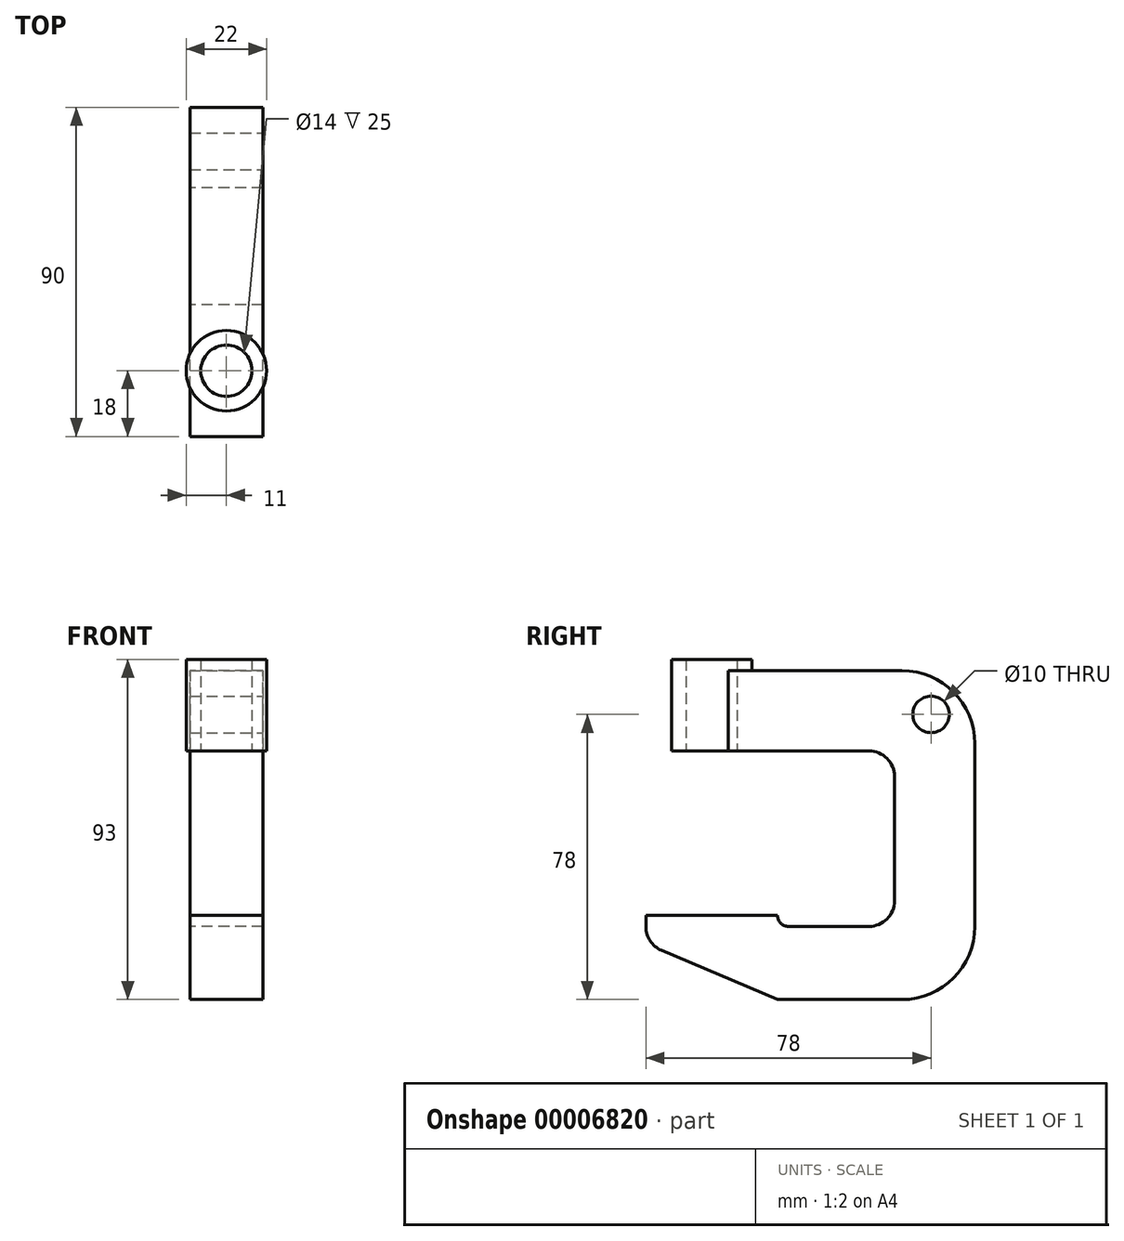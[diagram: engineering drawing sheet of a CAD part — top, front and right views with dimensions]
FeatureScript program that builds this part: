
annotation { "Feature Type Name" : "Feature", "Feature Type Description" : "" }
export const myFeature = defineFeature(function(context is Context, id is Id, definition is map)
    precondition{}
    {
        {
            var Q0;
            Q0=qCreatedBy(makeId("Right.planeOp"),FACE);
            var sketch = newSketch(context, id + "F0", { "sketchPlane" : qUnion([Q0])});
            skLineSegment(sketch, "E0", {"start": v(0, 0) * mm, "end": v(0, -3.09) * mm});
            skLineSegment(sketch, "E1", {"start": v(4.26, -9.53) * mm, "end": v(36, -23) * mm});
            skLineSegment(sketch, "E2", {"start": v(36, -23) * mm, "end": v(70, -23) * mm});
            skLineSegment(sketch, "E3", {"start": v(90, -3) * mm, "end": v(90, 47) * mm});
            skLineSegment(sketch, "E4", {"start": v(70, 67) * mm, "end": v(7, 67) * mm});
            skLineSegment(sketch, "E5", {"start": v(7, 67) * mm, "end": v(7, 45) * mm});
            skLineSegment(sketch, "E6", {"start": v(7, 45) * mm, "end": v(61, 45) * mm});
            skLineSegment(sketch, "E7", {"start": v(68, 38) * mm, "end": v(68, 4) * mm});
            skLineSegment(sketch, "E8", {"start": v(61, -3) * mm, "end": v(36, -3) * mm});
            skLineSegment(sketch, "E9", {"start": v(36, -3) * mm, "end": v(36, 0) * mm});
            skLineSegment(sketch, "E10", {"start": v(36, 0) * mm, "end": v(0, 0) * mm});
            skLineSegment(sketch, "E11", {"start": v(36, -23) * mm, "end": v(21.85, -23) * mm, "construction": true});
            skPoint(sketch, "E12.visualSharp", {"position": v(90, -23) * mm});
            skArc(sketch, "E12.filletArc", {"start": v(70, -23) * mm, "mid": v(84.14, -17.14) * mm, "end": v(90, -3) * mm});
            skPoint(sketch, "E13.visualSharp", {"position": v(90, 67) * mm});
            skArc(sketch, "E13.filletArc", {"start": v(90, 47) * mm, "mid": v(84.14, 61.14) * mm, "end": v(70, 67) * mm});
            skPoint(sketch, "E14.visualSharp", {"position": v(68, 45) * mm});
            skArc(sketch, "E14.filletArc", {"start": v(68, 38) * mm, "mid": v(65.95, 42.95) * mm, "end": v(61, 45) * mm});
            skPoint(sketch, "E15.visualSharp", {"position": v(68, -3) * mm});
            skArc(sketch, "E15.filletArc", {"start": v(61, -3) * mm, "mid": v(65.95, -0.95) * mm, "end": v(68, 4) * mm});
            skPoint(sketch, "E16.visualSharp", {"position": v(0, -7.72) * mm});
            skArc(sketch, "E16.filletArc", {"start": v(0, -3.09) * mm, "mid": v(1.16, -6.95) * mm, "end": v(4.26, -9.53) * mm});
            skSolve(sketch);
        }
        {
            var Q0;
            Q0 = qSketchRegion(id + "F0", true);
            extrude(context, id + "F1", {"entities" : qUnion([Q0]), "endBound" : BoundingType.SYMMETRIC, "depth" : 20 * mm});
        }
        {
            var Q0;
            Q0=makeQuery(id+"F1.opExtrude","SWEPT_FACE",FACE,{"disambiguationData":[OSD([sQuery(id+"F0.wireOp",EDGE,"E6")])]});
            var sketch = newSketch(context, id + "F2", { "sketchPlane" : qUnion([Q0])});
            skCircle(sketch, "E17", {"center": v(0, -18) * mm, "radius": 11 * mm});
            skCircle(sketch, "E18", {"center": v(0, -18) * mm, "radius": 7 * mm});
            skSolve(sketch);
        }
        {
            var Q0;
            Q0 = qSketchRegion(id + "F2", true);
            extrude(context, id + "F3", {"entities" : qUnion([Q0]), "operationType" : NewBodyOperationType.ADD, "oppositeDirection" : true, "depth" : 25 * mm});
        }
        {
            var Q0;
            Q0=makeQuery(id+"F3.boolean.opBoolean","SPLIT",FACE,{"disambiguationData":[TD([makeQuery(id+"F3.opExtrude","SWEPT_FACE",FACE,{"disambiguationData":[OSD([sQuery(id+"F2.wireOp",EDGE,"E18")])]})])],"derivedFrom":makeQuery(id+"F1.opExtrude","SWEPT_FACE",FACE,{"disambiguationData":[OSD([sQuery(id+"F0.wireOp",EDGE,"E4")])]})});
            var sketch = newSketch(context, id + "F4", { "sketchPlane" : qUnion([Q0])});
            skCircle(sketch, "E19.0", {"center": v(0, 18) * mm, "radius": 7 * mm});
            skSolve(sketch);
        }
        {
            var Q0;
            Q0 = qSketchRegion(id + "F4", true);
            extrude(context, id + "F5", {"entities" : qUnion([Q0]), "operationType" : NewBodyOperationType.REMOVE, "oppositeDirection" : true, "depth" : 25 * mm});
        }
        {
            var Q0;
            {var subQ0=sQuery(id+"F0.wireOp",EDGE,"E4");var subQ1=makeQuery(id+"F1.opExtrude","SWEPT_FACE",FACE,{"disambiguationData":[OSD([subQ0])]});var subQ2=sQuery(id+"F0.wireOp",EDGE,"E5");Q0=makeQuery(id+"F3.boolean.opBoolean","SPLIT",FACE,{"disambiguationData":[TD([makeQuery(id+"F1.opExtrude","CAP_FACE",FACE,{"disambiguationData":[OSD([sQuery(id+"F0.wireOp",EDGE,"E0"),sQuery(id+"F0.wireOp",EDGE,"E1"),sQuery(id+"F0.wireOp",EDGE,"E2"),sQuery(id+"F0.wireOp",EDGE,"E3"),subQ0,subQ2,sQuery(id+"F0.wireOp",EDGE,"E6"),sQuery(id+"F0.wireOp",EDGE,"E7"),sQuery(id+"F0.wireOp",EDGE,"E8"),sQuery(id+"F0.wireOp",EDGE,"E9"),sQuery(id+"F0.wireOp",EDGE,"E10"),sQuery(id+"F0.wireOp",EDGE,"E12.filletArc"),sQuery(id+"F0.wireOp",EDGE,"E13.filletArc"),sQuery(id+"F0.wireOp",EDGE,"E14.filletArc"),sQuery(id+"F0.wireOp",EDGE,"E15.filletArc"),sQuery(id+"F0.wireOp",EDGE,"E16.filletArc")])],"isStart":false}),subQ1,makeQuery(id+"F1.opExtrude","SWEPT_FACE",FACE,{"disambiguationData":[OSD([subQ2])]}),makeQuery(id+"F3.opExtrude","SWEPT_FACE",FACE,{"disambiguationData":[OSD([sQuery(id+"F2.wireOp",EDGE,"E17")])]})])],"derivedFrom":subQ1});}
            var sketch = newSketch(context, id + "F6", { "sketchPlane" : qUnion([Q0])});
            skLineSegment(sketch, "E20.1.0", {"start": v(-10, 7) * mm, "end": v(0, 7) * mm});
            skArc(sketch, "E20.1.1", {"start": v(0, 7) * mm, "mid": v(-5.94, 8.74) * mm, "end": v(-10, 13.42) * mm});
            skLineSegment(sketch, "E20.1.2", {"start": v(-10, 13.42) * mm, "end": v(-10, 7) * mm});
            skSolve(sketch);
        }
        {
            var Q0;
            Q0 = qSketchRegion(id + "F6", true);
            extrude(context, id + "F7", {"entities" : qUnion([Q0]), "operationType" : NewBodyOperationType.REMOVE, "oppositeDirection" : true, "depth" : 25 * mm});
        }
        {
            var Q0;
            {var subQ0=sQuery(id+"F0.wireOp",EDGE,"E4");var subQ1=makeQuery(id+"F1.opExtrude","SWEPT_FACE",FACE,{"disambiguationData":[OSD([subQ0])]});var subQ2=sQuery(id+"F0.wireOp",EDGE,"E5");Q0=makeQuery(id+"F3.boolean.opBoolean","SPLIT",FACE,{"disambiguationData":[TD([makeQuery(id+"F1.opExtrude","CAP_FACE",FACE,{"disambiguationData":[OSD([sQuery(id+"F0.wireOp",EDGE,"E0"),sQuery(id+"F0.wireOp",EDGE,"E1"),sQuery(id+"F0.wireOp",EDGE,"E2"),sQuery(id+"F0.wireOp",EDGE,"E3"),subQ0,subQ2,sQuery(id+"F0.wireOp",EDGE,"E6"),sQuery(id+"F0.wireOp",EDGE,"E7"),sQuery(id+"F0.wireOp",EDGE,"E8"),sQuery(id+"F0.wireOp",EDGE,"E9"),sQuery(id+"F0.wireOp",EDGE,"E10"),sQuery(id+"F0.wireOp",EDGE,"E12.filletArc"),sQuery(id+"F0.wireOp",EDGE,"E13.filletArc"),sQuery(id+"F0.wireOp",EDGE,"E14.filletArc"),sQuery(id+"F0.wireOp",EDGE,"E15.filletArc"),sQuery(id+"F0.wireOp",EDGE,"E16.filletArc")])],"isStart":false}),subQ1,makeQuery(id+"F1.opExtrude","SWEPT_FACE",FACE,{"disambiguationData":[OSD([subQ2])]}),makeQuery(id+"F3.opExtrude","SWEPT_FACE",FACE,{"disambiguationData":[OSD([sQuery(id+"F2.wireOp",EDGE,"E17")])]})])],"derivedFrom":subQ1});}
            var sketch = newSketch(context, id + "F8", { "sketchPlane" : qUnion([Q0])});
            skArc(sketch, "E21.0", {"start": v(10, 13.42) * mm, "mid": v(5.94, 8.74) * mm, "end": v(0, 7) * mm});
            skLineSegment(sketch, "E22", {"start": v(10, 13.42) * mm, "end": v(10, 7) * mm});
            skLineSegment(sketch, "E23", {"start": v(10, 7) * mm, "end": v(0, 7) * mm});
            skSolve(sketch);
        }
        {
            var Q0;
            Q0 = qSketchRegion(id + "F8", true);
            extrude(context, id + "F9", {"entities" : qUnion([Q0]), "operationType" : NewBodyOperationType.REMOVE, "oppositeDirection" : true, "depth" : 25 * mm});
        }
        {
            var Q0;
            Q0=makeQuery(id+"F1.opExtrude","SWEPT_EDGE",EDGE,{"disambiguationData":[OSD([sQuery(id+"F0.wireOp",EDGE,"E8"),sQuery(id+"F0.wireOp",EDGE,"E9")])]});
            fillet(context, id + "F10", {"entities" : qUnion([Q0]), "radius" : 3 * mm, "tangentPropagation" : true, "allowEdgeOverflow" : false});
        }
        {
            var Q0;
            Q0=qCreatedBy(makeId("Right.planeOp"),FACE);
            var sketch = newSketch(context, id + "F11", { "sketchPlane" : qUnion([Q0])});
            skLineSegment(sketch, "E24", {"start": v(11, 100) * mm, "end": v(7, 100) * mm});
            skLineSegment(sketch, "E25", {"start": v(7, 100) * mm, "end": v(7, 118) * mm});
            skLineSegment(sketch, "E26", {"start": v(7, 118) * mm, "end": v(18, 118) * mm});
            skLineSegment(sketch, "E27", {"start": v(18, 118) * mm, "end": v(18, 35) * mm});
            skLineSegment(sketch, "E28", {"start": v(11, 100) * mm, "end": v(11, 35) * mm});
            skLineSegment(sketch, "E29", {"start": v(11, 35) * mm, "end": v(18, 35) * mm});
            skSolve(sketch);
        }
        {
            var Q0;
            Q0 = qSketchRegion(id + "F11", true);
            var Q1;
            Q1=sQuery(id+"F11.wireOp",EDGE,"E27");
            revolve(context, id + "F12", {"entities" : qUnion([Q0]), "axis" : qUnion([Q1]), "revolveType" : RevolveType.FULL});
        }
        {
            var Q0;
            Q0=makeQuery(id+"F12.opRevolve","SWEPT_EDGE",EDGE,{"disambiguationData":[OSD([sQuery(id+"F11.wireOp",EDGE,"E25"),sQuery(id+"F11.wireOp",EDGE,"E26")])]});
            chamfer(context, id + "F13", {"entities" : qUnion([Q0]), "width" : 2 * mm, "tangentPropagation" : true});
        }
        {
            var Q0;
            Q0=makeQuery(id+"F12.opRevolve","SWEPT_FACE",FACE,{"disambiguationData":[OSD([sQuery(id+"F11.wireOp",EDGE,"E29")])]});
            var sketch = newSketch(context, id + "F14", { "sketchPlane" : qUnion([Q0])});
            skCircle(sketch, "E30", {"center": v(0, -18) * mm, "radius": 5 * mm});
            skSolve(sketch);
        }
        {
            var Q0;
            Q0 = qSketchRegion(id + "F14", true);
            extrude(context, id + "F15", {"entities" : qUnion([Q0]), "operationType" : NewBodyOperationType.ADD, "depth" : 2 * mm});
        }
        {
            var Q0;
            Q0=makeQuery(id+"F15.opExtrude","CAP_FACE",FACE,{"disambiguationData":[OSD([sQuery(id+"F14.wireOp",EDGE,"E30")])],"isStart":false});
            var sketch = newSketch(context, id + "F16", { "sketchPlane" : qUnion([Q0])});
            skCircle(sketch, "E31", {"center": v(0, -18) * mm, "radius": 3 * mm});
            skSolve(sketch);
        }
        {
            var Q0;
            Q0 = qSketchRegion(id + "F16", true);
            extrude(context, id + "F17", {"entities" : qUnion([Q0]), "operationType" : NewBodyOperationType.ADD, "depth" : 8 * mm});
        }
        {
            var Q0;
            Q0=qCreatedBy(makeId("Right.planeOp"),FACE);
            var sketch = newSketch(context, id + "F18", { "sketchPlane" : qUnion([Q0])});
            skCircle(sketch, "E32", {"center": v(18, 109) * mm, "radius": 5 * mm});
            skSolve(sketch);
        }
        {
            var Q0;
            Q0 = qSketchRegion(id + "F18", true);
            extrude(context, id + "F19", {"entities" : qUnion([Q0]), "operationType" : NewBodyOperationType.REMOVE, "oppositeDirection" : true, "depth" : 25 * mm});
        }
        {
            var Q0;
            Q0=makeQuery(id+"F19.boolean.opBoolean","COPY",FACE,{"derivedFrom":makeQuery(id+"F19.opExtrude","CAP_FACE",FACE,{"disambiguationData":[OSD([sQuery(id+"F18.wireOp",EDGE,"E32")])],"isStart":true})});
            var sketch = newSketch(context, id + "F20", { "sketchPlane" : qUnion([Q0])});
            skCircle(sketch, "E33.0", {"center": v(-18, 109) * mm, "radius": 5 * mm});
            skSolve(sketch);
        }
        {
            var Q0;
            Q0 = qSketchRegion(id + "F20", true);
            extrude(context, id + "F21", {"entities" : qUnion([Q0]), "operationType" : NewBodyOperationType.REMOVE, "oppositeDirection" : true, "depth" : 25 * mm});
        }
        {
            var Q0;
            Q0=qCreatedBy(makeId("Right.planeOp"),FACE);
            var sketch = newSketch(context, id + "F22", { "sketchPlane" : qUnion([Q0])});
            skCircle(sketch, "E34.0", {"center": v(18, 109) * mm, "radius": 5 * mm});
            skSolve(sketch);
        }
        {
            var Q0;
            Q0 = qSketchRegion(id + "F22", true);
            extrude(context, id + "F23", {"entities" : qUnion([Q0]), "endBound" : BoundingType.SYMMETRIC, "depth" : 89 * mm});
        }
        {
            var Q0;
            Q0=makeQuery(id+"F23.opExtrude","CAP_FACE",FACE,{"disambiguationData":[OSD([sQuery(id+"F22.wireOp",EDGE,"E34.0")])],"isStart":false});
            var sketch = newSketch(context, id + "F24", { "sketchPlane" : qUnion([Q0])});
            skCircle(sketch, "E35", {"center": v(18, 109) * mm, "radius": 3 * mm});
            skSolve(sketch);
        }
        {
            var Q0;
            Q0 = qSketchRegion(id + "F24", true);
            extrude(context, id + "F25", {"entities" : qUnion([Q0]), "operationType" : NewBodyOperationType.ADD, "depth" : 12 * mm});
        }
        {
            var Q0;
            Q0=makeQuery(id+"F23.opExtrude","CAP_FACE",FACE,{"disambiguationData":[OSD([sQuery(id+"F22.wireOp",EDGE,"E34.0")])],"isStart":true});
            var sketch = newSketch(context, id + "F26", { "sketchPlane" : qUnion([Q0])});
            skCircle(sketch, "E36", {"center": v(-18, 109) * mm, "radius": 3 * mm});
            skSolve(sketch);
        }
        {
            var Q0;
            Q0 = qSketchRegion(id + "F26", true);
            extrude(context, id + "F27", {"entities" : qUnion([Q0]), "operationType" : NewBodyOperationType.ADD, "depth" : 12 * mm});
        }
        {
            var Q0;
            Q0=makeQuery(id+"F25.opExtrude","CAP_FACE",FACE,{"disambiguationData":[OSD([sQuery(id+"F24.wireOp",EDGE,"E35")])],"isStart":false});
            var sketch = newSketch(context, id + "F28", { "sketchPlane" : qUnion([Q0])});
            skCircle(sketch, "E37.0", {"center": v(18, 109) * mm, "radius": 3 * mm});
            skCircle(sketch, "E38", {"center": v(18, 109) * mm, "radius": 10 * mm});
            skSolve(sketch);
        }
        {
            var Q0;
            Q0 = qSketchRegion(id + "F28", true);
            extrude(context, id + "F29", {"entities" : qUnion([Q0]), "oppositeDirection" : true, "depth" : 10 * mm});
        }
        {
            var Q0;
            Q0=makeQuery(id+"F29.opExtrude","CAP_EDGE",EDGE,{"disambiguationData":[OSD([sQuery(id+"F28.wireOp",EDGE,"E38")])],"isStart":true});
            var Q1;
            Q1=makeQuery(id+"F29.opExtrude","CAP_EDGE",EDGE,{"disambiguationData":[OSD([sQuery(id+"F28.wireOp",EDGE,"E38")])],"isStart":false});
            chamfer(context, id + "F30", {"entities" : qUnion([Q0, Q1]), "width" : 2 * mm, "tangentPropagation" : true});
        }
        {
            var Q0;
            Q0=makeQuery(id+"F29.opExtrude","SWEPT_BODY",BODY,{"disambiguationData":[OSD([sQuery(id+"F28.wireOp",EDGE,"E37.0"),sQuery(id+"F28.wireOp",EDGE,"E38")])]});
            var Q1;
            Q1=qCreatedBy(makeId("Right.planeOp"),FACE);
            mirror(context, id + "F31", {"entities" : qUnion([Q0]), "mirrorPlane" : qUnion([Q1])});
        }
        {
            var Q0;
            Q0=qCreatedBy(makeId("Right.planeOp"),FACE);
            var sketch = newSketch(context, id + "F32", { "sketchPlane" : qUnion([Q0])});
            skLineSegment(sketch, "E39", {"start": v(21, 30) * mm, "end": v(21, 32) * mm});
            skLineSegment(sketch, "E40", {"start": v(34.36, 22) * mm, "end": v(36.5, 22) * mm});
            skArc(sketch, "E41", {"start": v(36.5, 22) * mm, "mid": v(30.47, 29.67) * mm, "end": v(21, 32) * mm});
            skArc(sketch, "E42.0", {"start": v(34.36, 22) * mm, "mid": v(29, 28.23) * mm, "end": v(21, 30) * mm});
            skLineSegment(sketch, "E43", {"start": v(18, 24.98) * mm, "end": v(18, 32) * mm});
            skSolve(sketch);
        }
        {
            var Q0;
            Q0 = qSketchRegion(id + "F32", true);
            var Q1;
            Q1=sQuery(id+"F32.wireOp",EDGE,"E43");
            revolve(context, id + "F33", {"entities" : qUnion([Q0]), "axis" : qUnion([Q1]), "revolveType" : RevolveType.FULL});
        }
        {
            var Q0;
            Q0=makeQuery(id+"F33.opRevolve","SWEPT_BODY",BODY,{"disambiguationData":[OSD([sQuery(id+"F32.wireOp",EDGE,"E39"),sQuery(id+"F32.wireOp",EDGE,"E40"),sQuery(id+"F32.wireOp",EDGE,"E41"),sQuery(id+"F32.wireOp",EDGE,"E42.0")])]});
            deleteBodies(context, id + "F34", {"entities" : qUnion([Q0])});
        }
        {
            var Q0;
            Q0=makeQuery(id+"F31.opPattern","COPY",BODY,{"derivedFrom":makeQuery(id+"F29.opExtrude","SWEPT_BODY",BODY,{"disambiguationData":[OSD([sQuery(id+"F28.wireOp",EDGE,"E37.0"),sQuery(id+"F28.wireOp",EDGE,"E38")])]}),"instanceName":"1"});
            deleteBodies(context, id + "F35", {"entities" : qUnion([Q0])});
        }
        {
            var Q0;
            Q0=makeQuery(id+"F29.opExtrude","SWEPT_BODY",BODY,{"disambiguationData":[OSD([sQuery(id+"F28.wireOp",EDGE,"E37.0"),sQuery(id+"F28.wireOp",EDGE,"E38")])]});
            deleteBodies(context, id + "F36", {"entities" : qUnion([Q0])});
        }
        {
            var Q0;
            Q0=makeQuery(id+"F23.opExtrude","SWEPT_BODY",BODY,{"disambiguationData":[OSD([sQuery(id+"F22.wireOp",EDGE,"E34.0")])]});
            deleteBodies(context, id + "F37", {"entities" : qUnion([Q0])});
        }
        {
            var Q0;
            Q0=makeQuery(id+"F12.opRevolve","SWEPT_BODY",BODY,{"disambiguationData":[OSD([sQuery(id+"F11.wireOp",EDGE,"E24"),sQuery(id+"F11.wireOp",EDGE,"E25"),sQuery(id+"F11.wireOp",EDGE,"E26"),sQuery(id+"F11.wireOp",EDGE,"E27"),sQuery(id+"F11.wireOp",EDGE,"E28"),sQuery(id+"F11.wireOp",EDGE,"E29")])]});
            deleteBodies(context, id + "F38", {"entities" : qUnion([Q0])});
        }
        {
            var Q0;
            {var subQ0=sQuery(id+"F0.wireOp",EDGE,"E0");var subQ1=sQuery(id+"F0.wireOp",EDGE,"E1");var subQ2=sQuery(id+"F0.wireOp",EDGE,"E2");var subQ3=sQuery(id+"F0.wireOp",EDGE,"E3");var subQ4=sQuery(id+"F0.wireOp",EDGE,"E4");var subQ5=sQuery(id+"F0.wireOp",EDGE,"E6");var subQ6=sQuery(id+"F0.wireOp",EDGE,"E7");var subQ7=sQuery(id+"F0.wireOp",EDGE,"E8");var subQ8=sQuery(id+"F0.wireOp",EDGE,"E9");var subQ9=sQuery(id+"F0.wireOp",EDGE,"E10");var subQ10=sQuery(id+"F0.wireOp",EDGE,"E12.filletArc");var subQ11=sQuery(id+"F0.wireOp",EDGE,"E13.filletArc");var subQ12=sQuery(id+"F0.wireOp",EDGE,"E14.filletArc");var subQ13=sQuery(id+"F0.wireOp",EDGE,"E15.filletArc");var subQ14=sQuery(id+"F0.wireOp",EDGE,"E16.filletArc");Q0=makeQuery(id+"F3.boolean.opBoolean","SPLIT",FACE,{"disambiguationData":[TD([makeQuery(id+"F1.opExtrude","SWEPT_FACE",FACE,{"disambiguationData":[OSD([subQ0])]})])],"derivedFrom":makeQuery(id+"F1.opExtrude","CAP_FACE",FACE,{"disambiguationData":[OSD([subQ0,subQ1,subQ2,subQ3,subQ4,sQuery(id+"F0.wireOp",EDGE,"E5"),subQ5,subQ6,subQ7,subQ8,subQ9,subQ10,subQ11,subQ12,subQ13,subQ14])],"isStart":false})});}
            var sketch = newSketch(context, id + "F39", { "sketchPlane" : qUnion([Q0])});
            skCircle(sketch, "E44", {"center": v(78, 55) * mm, "radius": 5 * mm});
            skSolve(sketch);
        }
        {
            var Q0;
            Q0 = qSketchRegion(id + "F39", true);
            extrude(context, id + "F40", {"entities" : qUnion([Q0]), "operationType" : NewBodyOperationType.REMOVE, "endBound" : BoundingType.THROUGH_ALL, "oppositeDirection" : true, "depth" : 25 * mm});
        }
    });
